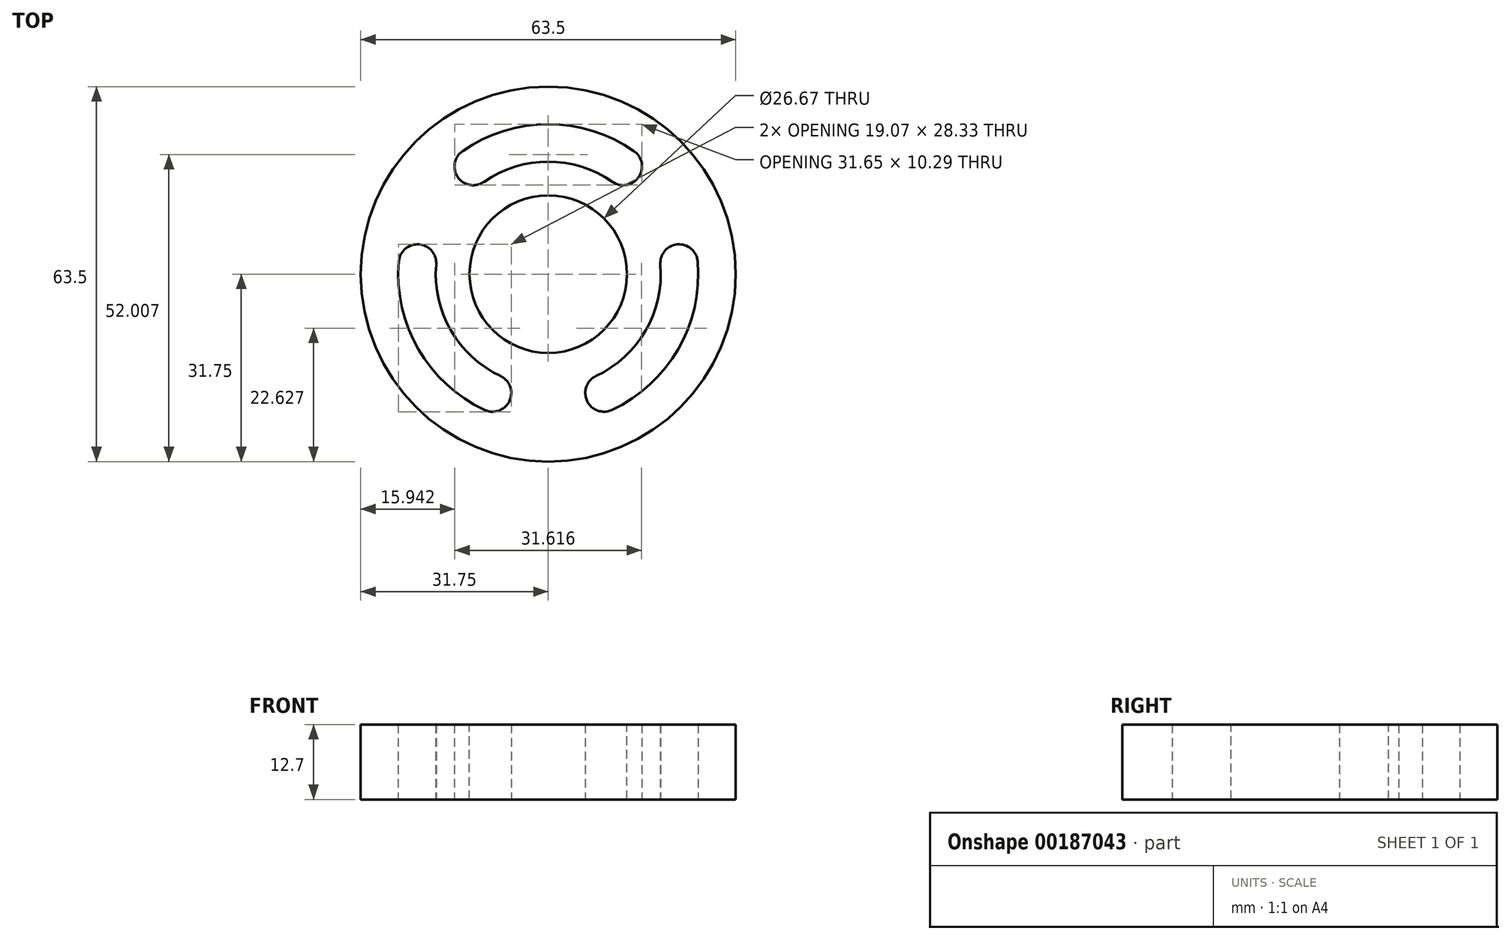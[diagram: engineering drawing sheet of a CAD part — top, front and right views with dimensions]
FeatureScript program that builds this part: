
annotation { "Feature Type Name" : "Feature", "Feature Type Description" : "" }
export const myFeature = defineFeature(function(context is Context, id is Id, definition is map)
    precondition{}
    {
        {
            var Q0;
            Q0=qCreatedBy(makeId("Top.planeOp"),FACE);
            var sketch = newSketch(context, id + "F0", { "sketchPlane" : qUnion([Q0])});
            skCircle(sketch, "E0.0", {"center": v(0, 0) * mm, "radius": 31.75 * mm});
            skCircle(sketch, "E1", {"center": v(0, 0) * mm, "radius": 22.23 * mm, "construction": true});
            skLineSegment(sketch, "E2", {"start": v(0, 0) * mm, "end": v(0, 22.23) * mm, "construction": true});
            skArc(sketch, "E3", {"start": v(-12.7, 18.24) * mm, "mid": v(0, 22.22) * mm, "end": v(12.7, 18.24) * mm});
            skArc(sketch, "E4.0.startCap", {"start": v(-10.89, 15.63) * mm, "mid": v(-15.3, 16.42) * mm, "end": v(-14.51, 20.84) * mm});
            skArc(sketch, "E4.0.endCap", {"start": v(14.51, 20.84) * mm, "mid": v(15.3, 16.42) * mm, "end": v(10.89, 15.63) * mm});
            skArc(sketch, "E4.0.left", {"start": v(-14.51, 20.84) * mm, "mid": v(0, 25.4) * mm, "end": v(14.51, 20.84) * mm});
            skArc(sketch, "E4.0.right", {"start": v(-10.89, 15.63) * mm, "mid": v(0, 19.05) * mm, "end": v(10.89, 15.63) * mm});
            skArc(sketch, "E5.1.0", {"start": v(-25.3, 2.15) * mm, "mid": v(-21.88, 5.04) * mm, "end": v(-18.98, 1.61) * mm});
            skArc(sketch, "E5.1.1", {"start": v(-10.8, -23) * mm, "mid": v(-22, -12.7) * mm, "end": v(-25.3, 2.15) * mm});
            skArc(sketch, "E5.1.2", {"start": v(-8.1, -17.24) * mm, "mid": v(-16.5, -9.52) * mm, "end": v(-18.98, 1.61) * mm});
            skArc(sketch, "E5.1.3", {"start": v(-8.1, -17.24) * mm, "mid": v(-6.57, -21.47) * mm, "end": v(-10.8, -23) * mm});
            skArc(sketch, "E5.1.4", {"start": v(-9.45, -20.12) * mm, "mid": v(-19.25, -11.11) * mm, "end": v(-22.15, 1.88) * mm});
            skArc(sketch, "E5.2.0", {"start": v(10.8, -23) * mm, "mid": v(6.57, -21.47) * mm, "end": v(8.1, -17.24) * mm});
            skArc(sketch, "E5.2.1", {"start": v(25.3, 2.15) * mm, "mid": v(22, -12.7) * mm, "end": v(10.8, -23) * mm});
            skArc(sketch, "E5.2.2", {"start": v(18.98, 1.61) * mm, "mid": v(16.5, -9.53) * mm, "end": v(8.1, -17.24) * mm});
            skArc(sketch, "E5.2.3", {"start": v(18.98, 1.61) * mm, "mid": v(21.88, 5.04) * mm, "end": v(25.3, 2.15) * mm});
            skArc(sketch, "E5.2.4", {"start": v(22.15, 1.88) * mm, "mid": v(19.25, -11.11) * mm, "end": v(9.45, -20.12) * mm});
            skSolve(sketch);
        }
        {
            var Q0;
            Q0=makeQuery(id+"F0.imprint","IMPRINT",FACE,{"disambiguationData":[TD([[makeQuery(id+"F0.imprint","IMPRINT",EDGE,{"derivedFrom":sQuery(id+"F0.wireOp",EDGE,"E0.0")}),1.0]])]});
            extrude(context, id + "F1", {"entities" : qUnion([Q0]), "depth" : 12.7 * mm});
        }
        {
            var Q0;
            Q0=makeQuery(id+"F1.opExtrude","CAP_FACE",FACE,{"disambiguationData":[OSD([sQuery(id+"F0.wireOp",EDGE,"E0.0"),sQuery(id+"F0.wireOp",EDGE,"E4.0.startCap"),sQuery(id+"F0.wireOp",EDGE,"E4.0.endCap"),sQuery(id+"F0.wireOp",EDGE,"E4.0.left"),sQuery(id+"F0.wireOp",EDGE,"E4.0.right"),sQuery(id+"F0.wireOp",EDGE,"E5.1.0"),sQuery(id+"F0.wireOp",EDGE,"E5.1.1"),sQuery(id+"F0.wireOp",EDGE,"E5.1.2"),sQuery(id+"F0.wireOp",EDGE,"E5.1.3"),sQuery(id+"F0.wireOp",EDGE,"E5.2.0"),sQuery(id+"F0.wireOp",EDGE,"E5.2.1"),sQuery(id+"F0.wireOp",EDGE,"E5.2.2"),sQuery(id+"F0.wireOp",EDGE,"E5.2.3")])],"isStart":false});
            var sketch = newSketch(context, id + "F2", { "sketchPlane" : qUnion([Q0])});
            skCircle(sketch, "E6", {"center": v(0, 0) * mm, "radius": 13.34 * mm});
            skSolve(sketch);
        }
        {
            var Q0;
            Q0 = qSketchRegion(id + "F2", true);
            extrude(context, id + "F3", {"entities" : qUnion([Q0]), "operationType" : NewBodyOperationType.REMOVE, "oppositeDirection" : true, "depth" : 25.4 * mm});
        }
    });
